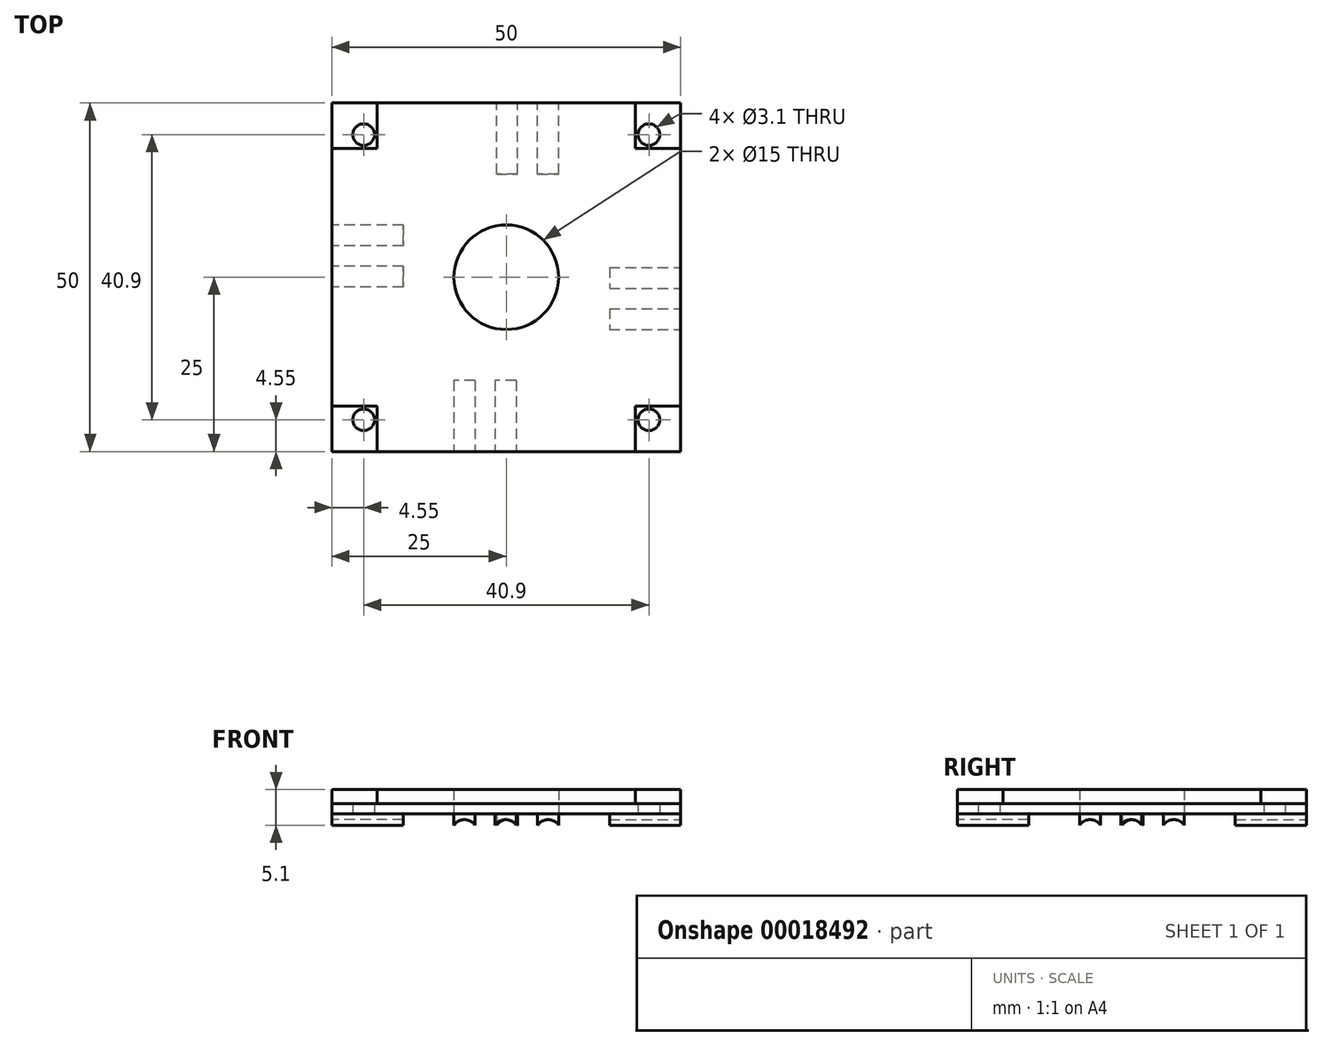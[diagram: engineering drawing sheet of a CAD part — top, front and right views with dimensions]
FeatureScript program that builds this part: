
annotation { "Feature Type Name" : "Feature", "Feature Type Description" : "" }
export const myFeature = defineFeature(function(context is Context, id is Id, definition is map)
    precondition{}
    {
        {
            var Q0;
            Q0=qCreatedBy(makeId("Top.planeOp"),FACE);
            var sketch = newSketch(context, id + "F0", { "sketchPlane" : qUnion([Q0])});
            skLineSegment(sketch, "E0.rect.bottom", {"start": v(25, 25) * mm, "end": v(-25, 25) * mm});
            skLineSegment(sketch, "E0.rect.top", {"start": v(25, -25) * mm, "end": v(-25, -25) * mm});
            skLineSegment(sketch, "E0.rect.left", {"start": v(25, 25) * mm, "end": v(25, -25) * mm});
            skLineSegment(sketch, "E0.rect.right", {"start": v(-25, 25) * mm, "end": v(-25, -25) * mm});
            skPoint(sketch, "E0.rect.middle", {"position": v(0, 0) * mm});
            skCircle(sketch, "E1", {"center": v(0, 0) * mm, "radius": 7.5 * mm});
            skCircle(sketch, "E2", {"center": v(-20.45, -20.45) * mm, "radius": 1.55 * mm});
            skCircle(sketch, "E3", {"center": v(-20.45, 20.45) * mm, "radius": 1.55 * mm});
            skCircle(sketch, "E4", {"center": v(20.45, 20.45) * mm, "radius": 1.55 * mm});
            skCircle(sketch, "E5", {"center": v(20.45, -20.45) * mm, "radius": 1.55 * mm});
            skSolve(sketch);
        }
        {
            var Q0;
            Q0 = qSketchRegion(id + "F0", true);
            extrude(context, id + "F1", {"entities" : qUnion([Q0]), "depth" : 1.5 * mm});
        }
        {
            var Q0;
            Q0=makeQuery(id+"F1.opExtrude","CAP_FACE",FACE,{"disambiguationData":[OSD([sQuery(id+"F0.wireOp",EDGE,"E0.rect.bottom"),sQuery(id+"F0.wireOp",EDGE,"E0.rect.top"),sQuery(id+"F0.wireOp",EDGE,"E0.rect.left"),sQuery(id+"F0.wireOp",EDGE,"E0.rect.right"),sQuery(id+"F0.wireOp",EDGE,"E1"),sQuery(id+"F0.wireOp",EDGE,"E2"),sQuery(id+"F0.wireOp",EDGE,"E3"),sQuery(id+"F0.wireOp",EDGE,"E4"),sQuery(id+"F0.wireOp",EDGE,"E5")])],"isStart":false});
            var sketch = newSketch(context, id + "F2", { "sketchPlane" : qUnion([Q0])});
            skLineSegment(sketch, "E6.rect.bottom", {"start": v(18.5, 25) * mm, "end": v(-18.5, 25) * mm});
            skLineSegment(sketch, "E6.rect.top", {"start": v(18.5, -25) * mm, "end": v(-18.5, -25) * mm});
            skLineSegment(sketch, "E6.rect.left", {"start": v(18.5, 25) * mm, "end": v(18.5, -25) * mm});
            skLineSegment(sketch, "E6.rect.right", {"start": v(-18.5, 25) * mm, "end": v(-18.5, -25) * mm});
            skPoint(sketch, "E6.rect.middle", {"position": v(0, 0) * mm});
            skLineSegment(sketch, "E7.rect.bottom", {"start": v(-25, 18.5) * mm, "end": v(25, 18.5) * mm});
            skLineSegment(sketch, "E7.rect.top", {"start": v(-25, -18.5) * mm, "end": v(25, -18.5) * mm});
            skLineSegment(sketch, "E7.rect.left", {"start": v(-25, 18.5) * mm, "end": v(-25, -18.5) * mm});
            skLineSegment(sketch, "E7.rect.right", {"start": v(25, 18.5) * mm, "end": v(25, -18.5) * mm});
            skSolve(sketch);
        }
        {
            var Q0;
            {var subQ6=sQuery(id+"F2.wireOp",EDGE,"E6.rect.bottom");Q0=makeQuery(id+"F2.imprint","IMPRINT",FACE,{"disambiguationData":[TD([[makeQuery(id+"F2.imprint","IMPRINT",EDGE,{"derivedFrom":subQ6}),1.0]])]});}
            var Q1;
            Q1=makeQuery(id+"F2.imprint","IMPRINT",FACE,{"disambiguationData":[TD([[makeQuery(id+"F2.imprint","IMPRINT",EDGE,{"derivedFrom":makeQuery(id+"F1.opExtrude","CAP_EDGE",EDGE,{"disambiguationData":[OSD([sQuery(id+"F0.wireOp",EDGE,"E1")])],"isStart":false})}),-1.0]])]});
            var Q2;
            {var subQ0=sQuery(id+"F2.wireOp",EDGE,"E7.rect.left");Q2=makeQuery(id+"F2.imprint","IMPRINT",FACE,{"disambiguationData":[TD([[makeQuery(id+"F2.imprint","IMPRINT",EDGE,{"derivedFrom":subQ0}),1.0]])]});}
            var Q3;
            {var subQ0=sQuery(id+"F2.wireOp",EDGE,"E7.rect.right");Q3=makeQuery(id+"F2.imprint","IMPRINT",FACE,{"disambiguationData":[TD([[makeQuery(id+"F2.imprint","IMPRINT",EDGE,{"derivedFrom":subQ0}),-1.0]])]});}
            var Q4;
            {var subQ6=sQuery(id+"F2.wireOp",EDGE,"E6.rect.top");Q4=makeQuery(id+"F2.imprint","IMPRINT",FACE,{"disambiguationData":[TD([[makeQuery(id+"F2.imprint","IMPRINT",EDGE,{"derivedFrom":subQ6}),-1.0]])]});}
            extrude(context, id + "F3", {"entities" : qUnion([Q0, Q1, Q2, Q3, Q4]), "depth" : 2 * mm});
        }
        {
            var Q0;
            Q0=makeQuery(id+"F1.opExtrude","SWEPT_FACE",FACE,{"disambiguationData":[OSD([sQuery(id+"F0.wireOp",EDGE,"E0.rect.top")])]});
            var sketch = newSketch(context, id + "F4", { "sketchPlane" : qUnion([Q0])});
            skLineSegment(sketch, "E8.rect.bottom", {"start": v(-7.5, 0) * mm, "end": v(-4.5, 0) * mm});
            skLineSegment(sketch, "E8.rect.left", {"start": v(-7.5, 0) * mm, "end": v(-7.5, -1.6) * mm});
            skLineSegment(sketch, "E8.rect.right", {"start": v(-4.5, 0) * mm, "end": v(-4.5, -1.6) * mm});
            skPoint(sketch, "E8.rect.middle", {"position": v(-6, -0.8) * mm});
            skLineSegment(sketch, "E9.rect.bottom", {"start": v(-1.6, 0) * mm, "end": v(1.4, 0) * mm});
            skLineSegment(sketch, "E9.rect.left", {"start": v(-1.6, 0) * mm, "end": v(-1.6, -1.6) * mm});
            skLineSegment(sketch, "E9.rect.right", {"start": v(1.4, 0) * mm, "end": v(1.4, -1.6) * mm});
            skPoint(sketch, "E9.rect.middle", {"position": v(-0.1, -0.8) * mm});
            skArc(sketch, "E10", {"start": v(1.4, -1.6) * mm, "mid": v(-0.1, -0.8) * mm, "end": v(-1.6, -1.6) * mm});
            skArc(sketch, "E11", {"start": v(-4.5, -1.6) * mm, "mid": v(-6, -0.8) * mm, "end": v(-7.5, -1.6) * mm});
            skSolve(sketch);
        }
        {
            var Q0;
            Q0=makeQuery(id+"F4.imprint","IMPRINT",FACE,{"disambiguationData":[TD([[makeQuery(id+"F4.imprint","IMPRINT",EDGE,{"derivedFrom":sQuery(id+"F4.wireOp",EDGE,"E8.rect.bottom")}),1.0]])]});
            var Q1;
            Q1=makeQuery(id+"F4.imprint","IMPRINT",FACE,{"disambiguationData":[TD([[makeQuery(id+"F4.imprint","IMPRINT",EDGE,{"derivedFrom":sQuery(id+"F4.wireOp",EDGE,"E9.rect.bottom")}),1.0]])]});
            extrude(context, id + "F5", {"entities" : qUnion([Q0, Q1]), "oppositeDirection" : true, "depth" : 10.2 * mm});
        }
        {
            var Q0;
            Q0=makeQuery(id+"F1.opExtrude","SWEPT_FACE",FACE,{"disambiguationData":[OSD([sQuery(id+"F0.wireOp",EDGE,"E0.rect.left")])]});
            var sketch = newSketch(context, id + "F6", { "sketchPlane" : qUnion([Q0])});
            skLineSegment(sketch, "E12.rect.bottom", {"start": v(-7.5, 0) * mm, "end": v(-4.5, 0) * mm});
            skLineSegment(sketch, "E12.rect.left", {"start": v(-7.5, 0) * mm, "end": v(-7.5, -1.6) * mm});
            skLineSegment(sketch, "E12.rect.right", {"start": v(-4.5, 0) * mm, "end": v(-4.5, -1.6) * mm});
            skPoint(sketch, "E12.rect.middle", {"position": v(-6, -0.8) * mm});
            skLineSegment(sketch, "E13.rect.bottom", {"start": v(-1.6, 0) * mm, "end": v(1.4, 0) * mm});
            skLineSegment(sketch, "E13.rect.left", {"start": v(-1.6, 0) * mm, "end": v(-1.6, -1.6) * mm});
            skLineSegment(sketch, "E13.rect.right", {"start": v(1.4, 0) * mm, "end": v(1.4, -1.6) * mm});
            skPoint(sketch, "E13.rect.middle", {"position": v(-0.1, -0.8) * mm});
            skArc(sketch, "E14", {"start": v(1.4, -1.6) * mm, "mid": v(-0.1, -0.8) * mm, "end": v(-1.6, -1.6) * mm});
            skArc(sketch, "E15", {"start": v(-4.5, -1.6) * mm, "mid": v(-6, -0.8) * mm, "end": v(-7.5, -1.6) * mm});
            skSolve(sketch);
        }
        {
            var Q0;
            Q0=makeQuery(id+"F6.imprint","IMPRINT",FACE,{"disambiguationData":[TD([[makeQuery(id+"F6.imprint","IMPRINT",EDGE,{"derivedFrom":sQuery(id+"F6.wireOp",EDGE,"E13.rect.bottom")}),1.0]])]});
            var Q1;
            Q1=makeQuery(id+"F6.imprint","IMPRINT",FACE,{"disambiguationData":[TD([[makeQuery(id+"F6.imprint","IMPRINT",EDGE,{"derivedFrom":sQuery(id+"F6.wireOp",EDGE,"E12.rect.bottom")}),1.0]])]});
            extrude(context, id + "F7", {"entities" : qUnion([Q0, Q1]), "oppositeDirection" : true, "depth" : 10.2 * mm});
        }
        {
            var Q0;
            Q0=makeQuery(id+"F1.opExtrude","SWEPT_FACE",FACE,{"disambiguationData":[OSD([sQuery(id+"F0.wireOp",EDGE,"E0.rect.right")])]});
            var sketch = newSketch(context, id + "F8", { "sketchPlane" : qUnion([Q0])});
            skLineSegment(sketch, "E16.rect.bottom", {"start": v(-7.5, 0) * mm, "end": v(-4.5, 0) * mm});
            skLineSegment(sketch, "E16.rect.left", {"start": v(-7.5, 0) * mm, "end": v(-7.5, -1.6) * mm});
            skLineSegment(sketch, "E16.rect.right", {"start": v(-4.5, 0) * mm, "end": v(-4.5, -1.6) * mm});
            skPoint(sketch, "E16.rect.middle", {"position": v(-6, -0.8) * mm});
            skLineSegment(sketch, "E17.rect.bottom", {"start": v(-1.6, 0) * mm, "end": v(1.4, 0) * mm});
            skLineSegment(sketch, "E17.rect.left", {"start": v(-1.6, 0) * mm, "end": v(-1.6, -1.6) * mm});
            skLineSegment(sketch, "E17.rect.right", {"start": v(1.4, 0) * mm, "end": v(1.4, -1.6) * mm});
            skPoint(sketch, "E17.rect.middle", {"position": v(-0.1, -0.8) * mm});
            skArc(sketch, "E18", {"start": v(1.4, -1.6) * mm, "mid": v(-0.1, -0.8) * mm, "end": v(-1.6, -1.6) * mm});
            skArc(sketch, "E19", {"start": v(-4.5, -1.6) * mm, "mid": v(-6, -0.8) * mm, "end": v(-7.5, -1.6) * mm});
            skSolve(sketch);
        }
        {
            var Q0;
            Q0=makeQuery(id+"F8.imprint","IMPRINT",FACE,{"disambiguationData":[TD([[makeQuery(id+"F8.imprint","IMPRINT",EDGE,{"derivedFrom":sQuery(id+"F8.wireOp",EDGE,"E16.rect.bottom")}),-1.0]])]});
            var Q1;
            Q1=makeQuery(id+"F8.imprint","IMPRINT",FACE,{"disambiguationData":[TD([[makeQuery(id+"F8.imprint","IMPRINT",EDGE,{"derivedFrom":sQuery(id+"F8.wireOp",EDGE,"E17.rect.bottom")}),-1.0]])]});
            extrude(context, id + "F9", {"entities" : qUnion([Q0, Q1]), "oppositeDirection" : true, "depth" : 10.2 * mm});
        }
        {
            var Q0;
            Q0=makeQuery(id+"F1.opExtrude","SWEPT_FACE",FACE,{"disambiguationData":[OSD([sQuery(id+"F0.wireOp",EDGE,"E0.rect.bottom")])]});
            var sketch = newSketch(context, id + "F10", { "sketchPlane" : qUnion([Q0])});
            skLineSegment(sketch, "E20.rect.bottom", {"start": v(-7.5, 0) * mm, "end": v(-4.5, 0) * mm});
            skLineSegment(sketch, "E20.rect.left", {"start": v(-7.5, 0) * mm, "end": v(-7.5, -1.6) * mm});
            skLineSegment(sketch, "E20.rect.right", {"start": v(-4.5, 0) * mm, "end": v(-4.5, -1.6) * mm});
            skPoint(sketch, "E20.rect.middle", {"position": v(-6, -0.8) * mm});
            skLineSegment(sketch, "E21.rect.bottom", {"start": v(-1.6, 0) * mm, "end": v(1.4, 0) * mm});
            skLineSegment(sketch, "E21.rect.left", {"start": v(-1.6, 0) * mm, "end": v(-1.6, -1.6) * mm});
            skLineSegment(sketch, "E21.rect.right", {"start": v(1.4, 0) * mm, "end": v(1.4, -1.6) * mm});
            skPoint(sketch, "E21.rect.middle", {"position": v(-0.1, -0.8) * mm});
            skArc(sketch, "E22", {"start": v(1.4, -1.6) * mm, "mid": v(-0.1, -0.8) * mm, "end": v(-1.6, -1.6) * mm});
            skArc(sketch, "E23", {"start": v(-4.5, -1.6) * mm, "mid": v(-6, -0.8) * mm, "end": v(-7.5, -1.6) * mm});
            skSolve(sketch);
        }
        {
            var Q0;
            Q0=makeQuery(id+"F10.imprint","IMPRINT",FACE,{"disambiguationData":[TD([[makeQuery(id+"F10.imprint","IMPRINT",EDGE,{"derivedFrom":sQuery(id+"F10.wireOp",EDGE,"E20.rect.bottom")}),-1.0]])]});
            var Q1;
            Q1=makeQuery(id+"F10.imprint","IMPRINT",FACE,{"disambiguationData":[TD([[makeQuery(id+"F10.imprint","IMPRINT",EDGE,{"derivedFrom":sQuery(id+"F10.wireOp",EDGE,"E21.rect.bottom")}),-1.0]])]});
            extrude(context, id + "F11", {"entities" : qUnion([Q0, Q1]), "oppositeDirection" : true, "depth" : 10.2 * mm});
        }
    });
